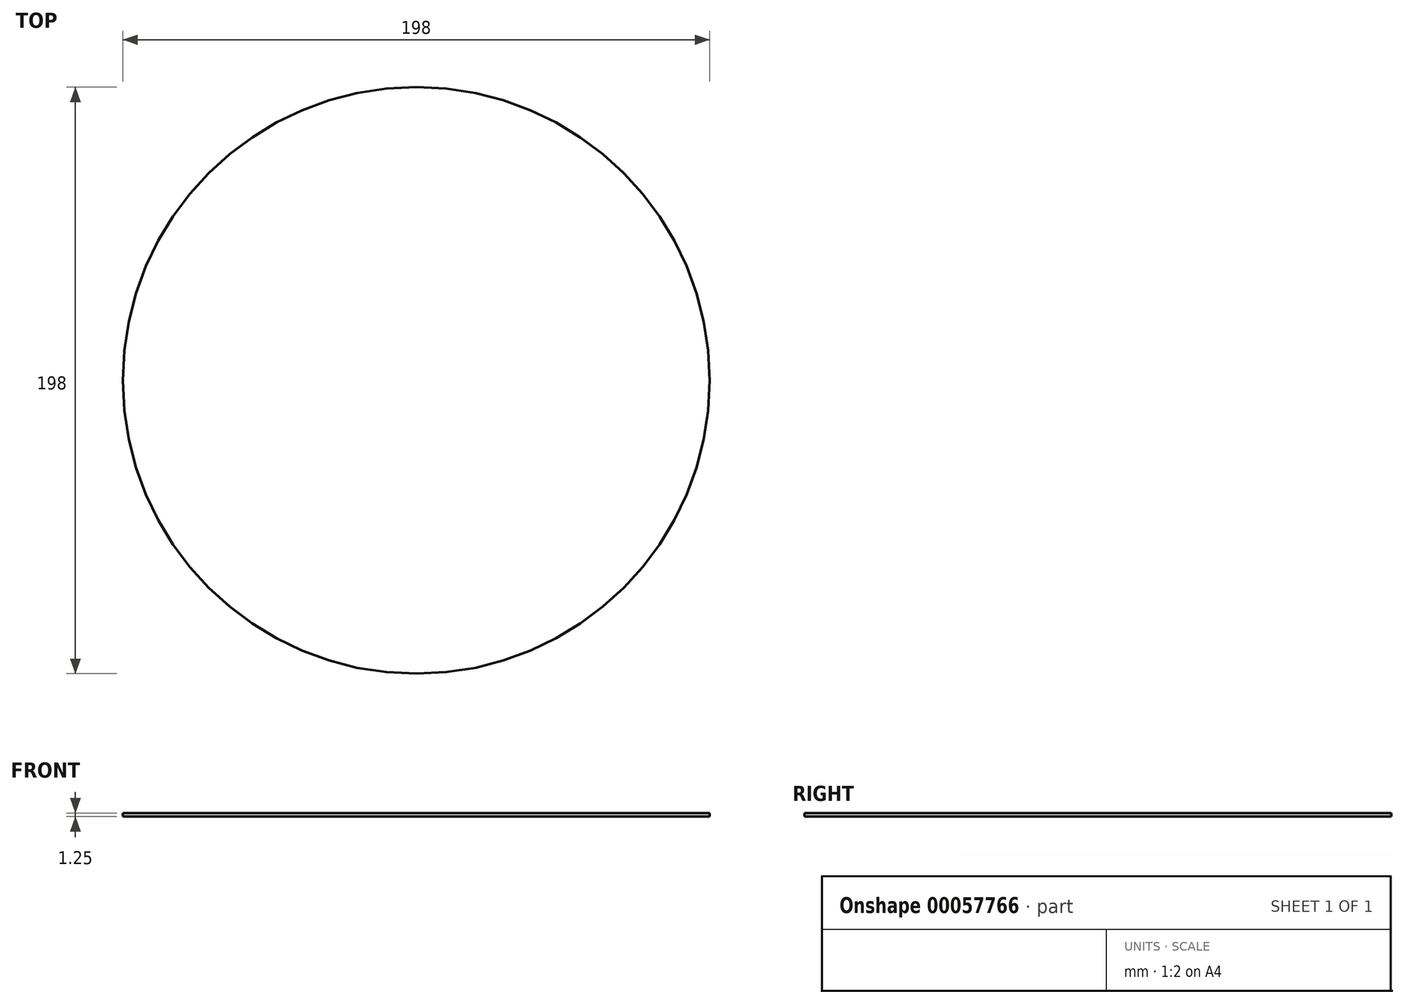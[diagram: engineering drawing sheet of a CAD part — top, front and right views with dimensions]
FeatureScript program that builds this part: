
annotation { "Feature Type Name" : "Feature", "Feature Type Description" : "" }
export const myFeature = defineFeature(function(context is Context, id is Id, definition is map)
    precondition{}
    {
        {
            var Q0;
            Q0=qCreatedBy(makeId("Top.planeOp"),FACE);
            var sketch = newSketch(context, id + "F0", { "sketchPlane" : qUnion([Q0])});
            skCircle(sketch, "E0", {"center": v(0, 0) * mm, "radius": 99 * mm});
            skSolve(sketch);
        }
        {
            var Q0;
            Q0=makeQuery(id+"F0.imprint","IMPRINT",FACE,{"disambiguationData":[TD([[makeQuery(id+"F0.imprint","IMPRINT",EDGE,{"derivedFrom":sQuery(id+"F0.wireOp",EDGE,"E0")}),1.0]])]});
            extrude(context, id + "F1", {"entities" : qUnion([Q0]), "depth" : 1.25 * mm});
        }
    });
